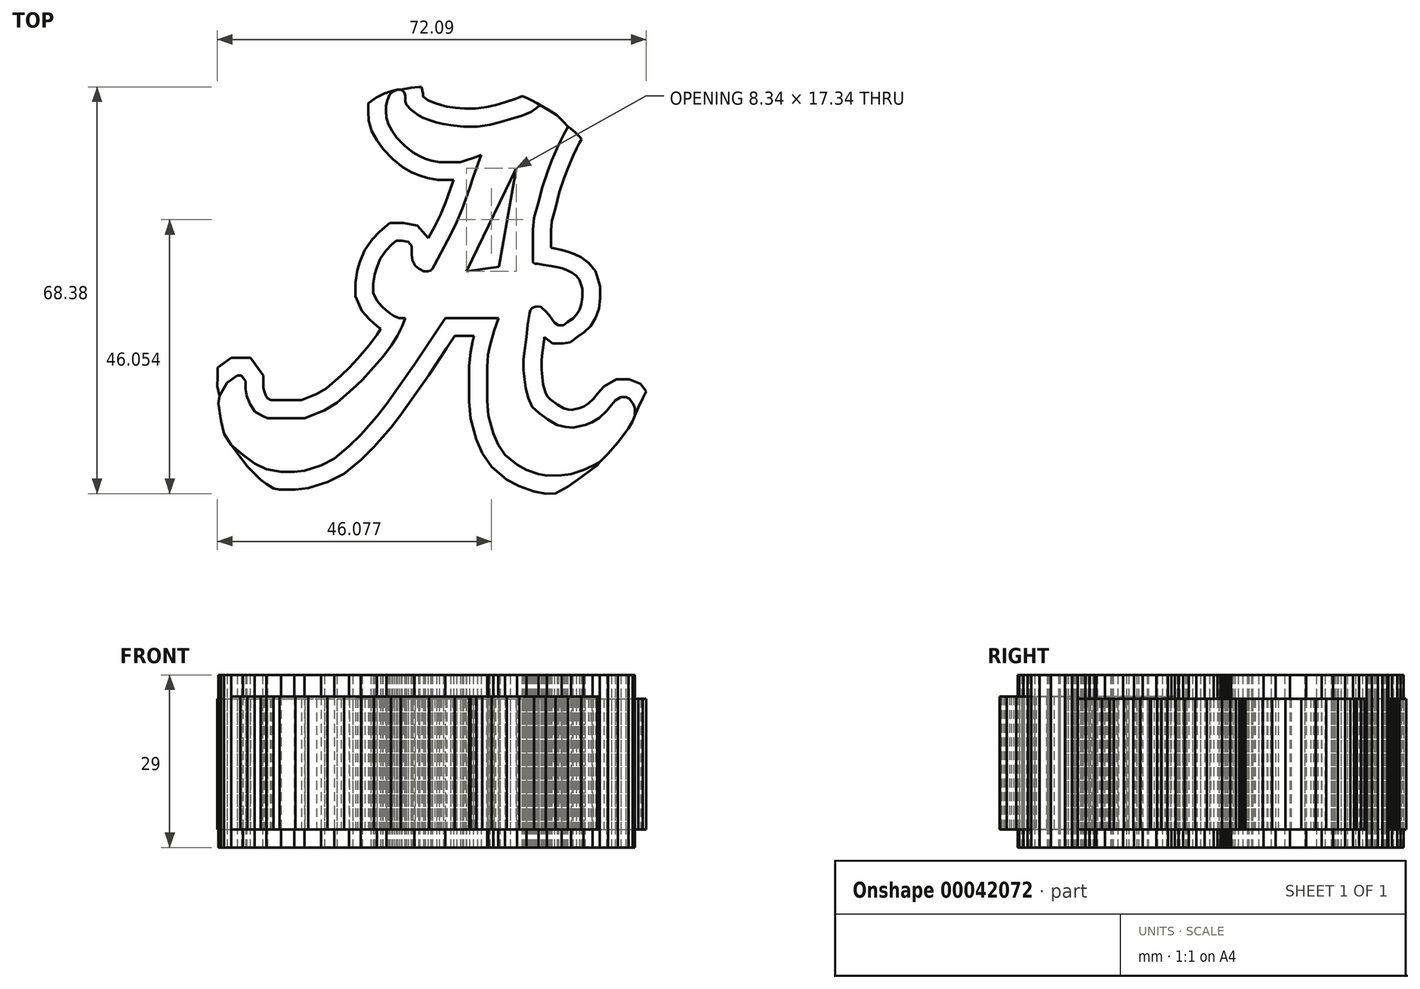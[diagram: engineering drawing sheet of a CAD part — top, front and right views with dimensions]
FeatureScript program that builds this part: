
annotation { "Feature Type Name" : "Feature", "Feature Type Description" : "" }
export const myFeature = defineFeature(function(context is Context, id is Id, definition is map)
    precondition{}
    {
        {
            var Q0;
            Q0=qCreatedBy(makeId("Top.planeOp"),FACE);
            var sketch = newSketch(context, id + "F0", { "sketchPlane" : qUnion([Q0])});
            skLineSegment(sketch, "E0", {"start": v(-56.78, -79.16) * mm, "end": v(-55.48, -76.91) * mm});
            skLineSegment(sketch, "E1", {"start": v(-55.48, -76.91) * mm, "end": v(-53.8, -75.71) * mm});
            skLineSegment(sketch, "E2", {"start": v(-53.8, -75.71) * mm, "end": v(-53.08, -75.71) * mm});
            skLineSegment(sketch, "E3", {"start": v(-53.08, -75.71) * mm, "end": v(-52.4, -76.66) * mm});
            skLineSegment(sketch, "E4", {"start": v(-52.4, -76.66) * mm, "end": v(-52.4, -78.02) * mm});
            skLineSegment(sketch, "E5", {"start": v(-52.4, -78.02) * mm, "end": v(-52.17, -79.12) * mm});
            skLineSegment(sketch, "E6", {"start": v(-52.17, -79.12) * mm, "end": v(-51.62, -80.55) * mm});
            skLineSegment(sketch, "E7", {"start": v(-51.62, -80.55) * mm, "end": v(-50.78, -81.82) * mm});
            skLineSegment(sketch, "E8", {"start": v(-50.78, -81.82) * mm, "end": v(-49.54, -82.5) * mm});
            skLineSegment(sketch, "E9", {"start": v(-49.54, -82.5) * mm, "end": v(-48.7, -82.86) * mm});
            skLineSegment(sketch, "E10", {"start": v(-48.7, -82.86) * mm, "end": v(-46.72, -82.86) * mm});
            skLineSegment(sketch, "E11", {"start": v(-46.72, -82.86) * mm, "end": v(-44.38, -82.86) * mm});
            skLineSegment(sketch, "E12", {"start": v(-44.38, -82.86) * mm, "end": v(-42.42, -82.86) * mm});
            skLineSegment(sketch, "E13", {"start": v(-42.42, -82.86) * mm, "end": v(-39.08, -81.54) * mm});
            skLineSegment(sketch, "E14", {"start": v(-39.08, -81.54) * mm, "end": v(-37.02, -80.29) * mm});
            skLineSegment(sketch, "E15", {"start": v(-37.02, -80.29) * mm, "end": v(-34.33, -77.96) * mm});
            skLineSegment(sketch, "E16", {"start": v(-34.33, -77.96) * mm, "end": v(-32.78, -76.5) * mm});
            skLineSegment(sketch, "E17", {"start": v(-32.78, -76.5) * mm, "end": v(-31.29, -74.85) * mm});
            skLineSegment(sketch, "E18", {"start": v(-31.29, -74.85) * mm, "end": v(-29.28, -72.52) * mm});
            skLineSegment(sketch, "E19", {"start": v(-29.28, -72.52) * mm, "end": v(-27.82, -70.57) * mm});
            skLineSegment(sketch, "E20", {"start": v(-27.82, -70.57) * mm, "end": v(-26.85, -69.02) * mm});
            skLineSegment(sketch, "E21", {"start": v(-26.85, -69.02) * mm, "end": v(-26.1, -67.53) * mm});
            skLineSegment(sketch, "E22", {"start": v(-26.1, -67.53) * mm, "end": v(-25.54, -66.05) * mm});
            skLineSegment(sketch, "E23", {"start": v(-25.54, -66.05) * mm, "end": v(-26.55, -66.05) * mm});
            skLineSegment(sketch, "E24", {"start": v(-26.55, -66.05) * mm, "end": v(-27.33, -65.75) * mm});
            skLineSegment(sketch, "E25", {"start": v(-27.33, -65.75) * mm, "end": v(-28.11, -65.26) * mm});
            skLineSegment(sketch, "E26", {"start": v(-28.11, -65.26) * mm, "end": v(-28.84, -64.67) * mm});
            skLineSegment(sketch, "E27", {"start": v(-28.84, -64.67) * mm, "end": v(-29.37, -64.14) * mm});
            skLineSegment(sketch, "E28", {"start": v(-29.37, -64.14) * mm, "end": v(-30.3, -63.15) * mm});
            skLineSegment(sketch, "E29", {"start": v(-30.3, -63.15) * mm, "end": v(-30.9, -61.77) * mm});
            skLineSegment(sketch, "E30", {"start": v(-30.9, -61.77) * mm, "end": v(-30.9, -60.3) * mm});
            skLineSegment(sketch, "E31", {"start": v(-30.9, -60.3) * mm, "end": v(-30.63, -58.7) * mm});
            skLineSegment(sketch, "E32", {"start": v(-30.63, -58.7) * mm, "end": v(-30.27, -57.51) * mm});
            skLineSegment(sketch, "E33", {"start": v(-30.27, -57.51) * mm, "end": v(-29.68, -56.03) * mm});
            skLineSegment(sketch, "E34", {"start": v(-29.68, -56.03) * mm, "end": v(-28.72, -54.68) * mm});
            skLineSegment(sketch, "E35", {"start": v(-28.72, -54.68) * mm, "end": v(-27.77, -53.7) * mm});
            skLineSegment(sketch, "E36", {"start": v(-27.77, -53.7) * mm, "end": v(-27.02, -53.04) * mm});
            skLineSegment(sketch, "E37", {"start": v(-27.02, -53.04) * mm, "end": v(-26.1, -53.04) * mm});
            skLineSegment(sketch, "E38", {"start": v(-26.1, -53.04) * mm, "end": v(-25.03, -53.24) * mm});
            skLineSegment(sketch, "E39", {"start": v(-25.03, -53.24) * mm, "end": v(-24.45, -53.91) * mm});
            skLineSegment(sketch, "E40", {"start": v(-24.45, -53.91) * mm, "end": v(-24.45, -54.89) * mm});
            skLineSegment(sketch, "E41", {"start": v(-24.45, -54.89) * mm, "end": v(-24.45, -55.44) * mm});
            skLineSegment(sketch, "E42", {"start": v(-24.45, -55.44) * mm, "end": v(-24.3, -56.31) * mm});
            skLineSegment(sketch, "E43", {"start": v(-24.3, -56.31) * mm, "end": v(-23.85, -57.26) * mm});
            skLineSegment(sketch, "E44", {"start": v(-23.85, -57.26) * mm, "end": v(-23.21, -57.73) * mm});
            skLineSegment(sketch, "E45", {"start": v(-23.21, -57.73) * mm, "end": v(-22.38, -58.21) * mm});
            skLineSegment(sketch, "E46", {"start": v(-22.38, -58.21) * mm, "end": v(-21.7, -58.21) * mm});
            skLineSegment(sketch, "E47", {"start": v(-21.7, -58.21) * mm, "end": v(-21.23, -58.04) * mm});
            skLineSegment(sketch, "E48", {"start": v(-21.23, -58.04) * mm, "end": v(-20.94, -57.73) * mm});
            skLineSegment(sketch, "E49", {"start": v(-20.94, -57.73) * mm, "end": v(-20.58, -57.05) * mm});
            skLineSegment(sketch, "E50", {"start": v(-20.58, -57.05) * mm, "end": v(-17.92, -52.02) * mm});
            skLineSegment(sketch, "E51", {"start": v(-17.92, -52.02) * mm, "end": v(-16.88, -49.93) * mm});
            skLineSegment(sketch, "E52", {"start": v(-16.88, -49.93) * mm, "end": v(-15.93, -47.62) * mm});
            skLineSegment(sketch, "E53", {"start": v(-15.93, -47.62) * mm, "end": v(-14.72, -44.27) * mm});
            skLineSegment(sketch, "E54", {"start": v(-14.72, -44.27) * mm, "end": v(-14.08, -42.31) * mm});
            skLineSegment(sketch, "E55", {"start": v(-14.08, -42.31) * mm, "end": v(-12.77, -38.62) * mm});
            skLineSegment(sketch, "E56", {"start": v(-12.77, -38.62) * mm, "end": v(-14.08, -39.13) * mm});
            skLineSegment(sketch, "E57", {"start": v(-14.08, -39.13) * mm, "end": v(-15.3, -39.54) * mm});
            skLineSegment(sketch, "E58", {"start": v(-15.3, -39.54) * mm, "end": v(-16.22, -39.8) * mm});
            skLineSegment(sketch, "E59", {"start": v(-16.22, -39.8) * mm, "end": v(-17.38, -39.8) * mm});
            skLineSegment(sketch, "E60", {"start": v(-17.38, -39.8) * mm, "end": v(-18.8, -39.8) * mm});
            skLineSegment(sketch, "E61", {"start": v(-18.8, -39.8) * mm, "end": v(-19.8, -39.8) * mm});
            skLineSegment(sketch, "E62", {"start": v(-19.8, -39.8) * mm, "end": v(-21.1, -39.57) * mm});
            skLineSegment(sketch, "E63", {"start": v(-21.1, -39.57) * mm, "end": v(-22.14, -39.26) * mm});
            skLineSegment(sketch, "E64", {"start": v(-22.14, -39.26) * mm, "end": v(-23.1, -38.83) * mm});
            skLineSegment(sketch, "E65", {"start": v(-23.1, -38.83) * mm, "end": v(-24.24, -38.2) * mm});
            skLineSegment(sketch, "E66", {"start": v(-24.24, -38.2) * mm, "end": v(-25.57, -37.13) * mm});
            skLineSegment(sketch, "E67", {"start": v(-25.57, -37.13) * mm, "end": v(-26.95, -35.69) * mm});
            skLineSegment(sketch, "E68", {"start": v(-26.95, -35.69) * mm, "end": v(-27.71, -34.57) * mm});
            skLineSegment(sketch, "E69", {"start": v(-27.71, -34.57) * mm, "end": v(-28.36, -33.43) * mm});
            skLineSegment(sketch, "E70", {"start": v(-28.36, -33.43) * mm, "end": v(-28.68, -32.32) * mm});
            skLineSegment(sketch, "E71", {"start": v(-28.68, -32.32) * mm, "end": v(-28.74, -31.26) * mm});
            skLineSegment(sketch, "E72", {"start": v(-28.74, -31.26) * mm, "end": v(-28.74, -30.32) * mm});
            skLineSegment(sketch, "E73", {"start": v(-28.74, -30.32) * mm, "end": v(-28.5, -29.39) * mm});
            skLineSegment(sketch, "E74", {"start": v(-28.5, -29.39) * mm, "end": v(-28.18, -28.54) * mm});
            skLineSegment(sketch, "E75", {"start": v(-28.18, -28.54) * mm, "end": v(-27.7, -28.04) * mm});
            skLineSegment(sketch, "E76", {"start": v(-27.7, -28.04) * mm, "end": v(-26.86, -27.64) * mm});
            skLineSegment(sketch, "E77", {"start": v(-26.86, -27.64) * mm, "end": v(-26.2, -27.64) * mm});
            skLineSegment(sketch, "E78", {"start": v(-26.2, -27.64) * mm, "end": v(-25.65, -28.15) * mm});
            skLineSegment(sketch, "E79", {"start": v(-25.65, -28.15) * mm, "end": v(-25.5, -28.75) * mm});
            skLineSegment(sketch, "E80", {"start": v(-25.5, -28.75) * mm, "end": v(-25.5, -29.6) * mm});
            skLineSegment(sketch, "E81", {"start": v(-25.5, -29.6) * mm, "end": v(-25.3, -30.2) * mm});
            skLineSegment(sketch, "E82", {"start": v(-25.3, -30.2) * mm, "end": v(-24.55, -31) * mm});
            skLineSegment(sketch, "E83", {"start": v(-24.55, -31) * mm, "end": v(-23.32, -31.94) * mm});
            skLineSegment(sketch, "E84", {"start": v(-23.32, -31.94) * mm, "end": v(-22.49, -32.39) * mm});
            skLineSegment(sketch, "E85", {"start": v(-22.49, -32.39) * mm, "end": v(-21.4, -32.76) * mm});
            skLineSegment(sketch, "E86", {"start": v(-21.4, -32.76) * mm, "end": v(-20.26, -33.15) * mm});
            skLineSegment(sketch, "E87", {"start": v(-20.26, -33.15) * mm, "end": v(-19.1, -33.43) * mm});
            skLineSegment(sketch, "E88", {"start": v(-19.1, -33.43) * mm, "end": v(-17.4, -33.67) * mm});
            skLineSegment(sketch, "E89", {"start": v(-17.4, -33.67) * mm, "end": v(-15.71, -33.84) * mm});
            skLineSegment(sketch, "E90", {"start": v(-15.71, -33.84) * mm, "end": v(-13.96, -33.84) * mm});
            skLineSegment(sketch, "E91", {"start": v(-13.96, -33.84) * mm, "end": v(-13.39, -33.84) * mm});
            skLineSegment(sketch, "E92", {"start": v(-13.39, -33.84) * mm, "end": v(-11.31, -33.52) * mm});
            skLineSegment(sketch, "E93", {"start": v(-11.31, -33.52) * mm, "end": v(-9.59, -33.13) * mm});
            skLineSegment(sketch, "E94", {"start": v(-9.59, -33.13) * mm, "end": v(-7.84, -32.61) * mm});
            skLineSegment(sketch, "E95", {"start": v(-7.84, -32.61) * mm, "end": v(-5.91, -32) * mm});
            skLineSegment(sketch, "E96", {"start": v(-5.91, -32) * mm, "end": v(-4.4, -31.38) * mm});
            skLineSegment(sketch, "E97", {"start": v(-4.4, -31.38) * mm, "end": v(-3.48, -30.75) * mm});
            skLineSegment(sketch, "E98", {"start": v(-3.48, -30.75) * mm, "end": v(-3.06, -30.35) * mm});
            skLineSegment(sketch, "E99", {"start": v(-3.06, -30.35) * mm, "end": v(-2.62, -30.35) * mm});
            skLineSegment(sketch, "E100", {"start": v(-2.62, -30.35) * mm, "end": v(-1.19, -31.17) * mm});
            skLineSegment(sketch, "E101", {"start": v(-1.19, -31.17) * mm, "end": v(0, -31.98) * mm});
            skLineSegment(sketch, "E102", {"start": v(0, -31.98) * mm, "end": v(1.02, -32.97) * mm});
            skLineSegment(sketch, "E103", {"start": v(1.02, -32.97) * mm, "end": v(1.87, -33.88) * mm});
            skLineSegment(sketch, "E104", {"start": v(1.87, -33.88) * mm, "end": v(1.15, -35.16) * mm});
            skLineSegment(sketch, "E105", {"start": v(1.15, -35.16) * mm, "end": v(0.63, -36.14) * mm});
            skLineSegment(sketch, "E106", {"start": v(0.63, -36.14) * mm, "end": v(0, -37.46) * mm});
            skLineSegment(sketch, "E107", {"start": v(0, -37.46) * mm, "end": v(-0.86, -39.54) * mm});
            skLineSegment(sketch, "E108", {"start": v(-0.86, -39.54) * mm, "end": v(-1.58, -41.4) * mm});
            skLineSegment(sketch, "E109", {"start": v(-1.58, -41.4) * mm, "end": v(-2.47, -44.03) * mm});
            skLineSegment(sketch, "E110", {"start": v(-2.47, -44.03) * mm, "end": v(-3.14, -46.76) * mm});
            skLineSegment(sketch, "E111", {"start": v(-3.14, -46.76) * mm, "end": v(-3.83, -49.14) * mm});
            skLineSegment(sketch, "E112", {"start": v(-3.83, -49.14) * mm, "end": v(-4.03, -51.18) * mm});
            skLineSegment(sketch, "E113", {"start": v(-4.03, -51.18) * mm, "end": v(-4.03, -53.63) * mm});
            skLineSegment(sketch, "E114", {"start": v(-4.03, -53.63) * mm, "end": v(-4.03, -55.63) * mm});
            skLineSegment(sketch, "E115", {"start": v(-4.03, -55.63) * mm, "end": v(-4.03, -56.36) * mm});
            skLineSegment(sketch, "E116", {"start": v(-4.03, -56.36) * mm, "end": v(-4.03, -56.69) * mm});
            skLineSegment(sketch, "E117", {"start": v(-4.03, -56.69) * mm, "end": v(-3.74, -56.9) * mm});
            skLineSegment(sketch, "E118", {"start": v(-3.74, -56.9) * mm, "end": v(-3.25, -56.9) * mm});
            skLineSegment(sketch, "E119", {"start": v(-3.25, -56.9) * mm, "end": v(-2.27, -57.1) * mm});
            skLineSegment(sketch, "E120", {"start": v(-2.27, -57.1) * mm, "end": v(-1.01, -57.3) * mm});
            skLineSegment(sketch, "E121", {"start": v(-1.01, -57.3) * mm, "end": v(0, -57.47) * mm});
            skLineSegment(sketch, "E122", {"start": v(0, -57.47) * mm, "end": v(0.87, -57.7) * mm});
            skLineSegment(sketch, "E123", {"start": v(0.87, -57.7) * mm, "end": v(1.67, -58.01) * mm});
            skLineSegment(sketch, "E124", {"start": v(1.67, -58.01) * mm, "end": v(2.56, -58.43) * mm});
            skLineSegment(sketch, "E125", {"start": v(2.56, -58.43) * mm, "end": v(3.27, -58.95) * mm});
            skLineSegment(sketch, "E126", {"start": v(3.27, -58.95) * mm, "end": v(3.79, -59.6) * mm});
            skLineSegment(sketch, "E127", {"start": v(3.79, -59.6) * mm, "end": v(3.98, -60.24) * mm});
            skLineSegment(sketch, "E128", {"start": v(3.98, -60.24) * mm, "end": v(4.24, -61.14) * mm});
            skLineSegment(sketch, "E129", {"start": v(4.24, -61.14) * mm, "end": v(4.24, -62.5) * mm});
            skLineSegment(sketch, "E130", {"start": v(4.24, -62.5) * mm, "end": v(4.1, -63.77) * mm});
            skLineSegment(sketch, "E131", {"start": v(4.1, -63.77) * mm, "end": v(3.75, -64.7) * mm});
            skLineSegment(sketch, "E132", {"start": v(3.75, -64.7) * mm, "end": v(3.27, -65.5) * mm});
            skLineSegment(sketch, "E133", {"start": v(3.27, -65.5) * mm, "end": v(2.67, -66.1) * mm});
            skLineSegment(sketch, "E134", {"start": v(2.67, -66.1) * mm, "end": v(1.82, -66.67) * mm});
            skLineSegment(sketch, "E135", {"start": v(1.82, -66.67) * mm, "end": v(1.06, -67.25) * mm});
            skLineSegment(sketch, "E136", {"start": v(1.06, -67.25) * mm, "end": v(0.8, -67.28) * mm});
            skLineSegment(sketch, "E137", {"start": v(0.8, -67.28) * mm, "end": v(0.25, -67.28) * mm});
            skLineSegment(sketch, "E138", {"start": v(0.25, -67.28) * mm, "end": v(-0.4, -66.8) * mm});
            skLineSegment(sketch, "E139", {"start": v(-0.4, -66.8) * mm, "end": v(-1.34, -65.52) * mm});
            skLineSegment(sketch, "E140", {"start": v(-1.34, -65.52) * mm, "end": v(-2, -64.82) * mm});
            skLineSegment(sketch, "E141", {"start": v(-2, -64.82) * mm, "end": v(-2.37, -64.45) * mm});
            skLineSegment(sketch, "E142", {"start": v(-2.37, -64.45) * mm, "end": v(-2.7, -64.18) * mm});
            skLineSegment(sketch, "E143", {"start": v(-2.7, -64.18) * mm, "end": v(-3.23, -64.11) * mm});
            skLineSegment(sketch, "E144", {"start": v(-3.23, -64.11) * mm, "end": v(-3.66, -64.13) * mm});
            skLineSegment(sketch, "E145", {"start": v(-3.66, -64.13) * mm, "end": v(-4.18, -64.33) * mm});
            skLineSegment(sketch, "E146", {"start": v(-4.18, -64.33) * mm, "end": v(-4.5, -64.75) * mm});
            skLineSegment(sketch, "E147", {"start": v(-4.5, -64.75) * mm, "end": v(-4.64, -65.28) * mm});
            skLineSegment(sketch, "E148", {"start": v(-4.64, -65.28) * mm, "end": v(-4.94, -67.2) * mm});
            skLineSegment(sketch, "E149", {"start": v(-4.94, -67.2) * mm, "end": v(-5.14, -69.25) * mm});
            skLineSegment(sketch, "E150", {"start": v(-5.14, -69.25) * mm, "end": v(-5.46, -71.5) * mm});
            skLineSegment(sketch, "E151", {"start": v(-5.46, -71.5) * mm, "end": v(-5.62, -72.96) * mm});
            skLineSegment(sketch, "E152", {"start": v(-5.62, -72.96) * mm, "end": v(-5.62, -74.84) * mm});
            skLineSegment(sketch, "E153", {"start": v(-5.62, -74.84) * mm, "end": v(-5.28, -77.85) * mm});
            skLineSegment(sketch, "E154", {"start": v(-5.28, -77.85) * mm, "end": v(-4.8, -79.5) * mm});
            skLineSegment(sketch, "E155", {"start": v(-4.8, -79.5) * mm, "end": v(-4.16, -80.97) * mm});
            skLineSegment(sketch, "E156", {"start": v(-4.16, -80.97) * mm, "end": v(-3.03, -82.02) * mm});
            skLineSegment(sketch, "E157", {"start": v(-3.03, -82.02) * mm, "end": v(-1.58, -83.1) * mm});
            skLineSegment(sketch, "E158", {"start": v(-1.58, -83.1) * mm, "end": v(0, -84.01) * mm});
            skLineSegment(sketch, "E159", {"start": v(0, -84.01) * mm, "end": v(1.41, -84.38) * mm});
            skLineSegment(sketch, "E160", {"start": v(1.41, -84.38) * mm, "end": v(2.69, -84.48) * mm});
            skLineSegment(sketch, "E161", {"start": v(2.69, -84.48) * mm, "end": v(4.7, -84.05) * mm});
            skLineSegment(sketch, "E162", {"start": v(4.7, -84.05) * mm, "end": v(5.86, -83.59) * mm});
            skLineSegment(sketch, "E163", {"start": v(5.86, -83.59) * mm, "end": v(7.11, -82.81) * mm});
            skLineSegment(sketch, "E164", {"start": v(7.11, -82.81) * mm, "end": v(8.32, -81.7) * mm});
            skLineSegment(sketch, "E165", {"start": v(8.32, -81.7) * mm, "end": v(9.13, -80.65) * mm});
            skLineSegment(sketch, "E166", {"start": v(9.13, -80.65) * mm, "end": v(9.8, -79.88) * mm});
            skLineSegment(sketch, "E167", {"start": v(9.8, -79.88) * mm, "end": v(10.75, -79.34) * mm});
            skLineSegment(sketch, "E168", {"start": v(10.75, -79.34) * mm, "end": v(11.55, -79.34) * mm});
            skLineSegment(sketch, "E169", {"start": v(11.55, -79.34) * mm, "end": v(12.12, -79.58) * mm});
            skLineSegment(sketch, "E170", {"start": v(12.12, -79.58) * mm, "end": v(12.77, -80.44) * mm});
            skLineSegment(sketch, "E171", {"start": v(12.77, -80.44) * mm, "end": v(13.1, -81.15) * mm});
            skLineSegment(sketch, "E172", {"start": v(13.1, -81.15) * mm, "end": v(13.1, -82.44) * mm});
            skLineSegment(sketch, "E173", {"start": v(13.1, -82.44) * mm, "end": v(12.73, -83.4) * mm});
            skLineSegment(sketch, "E174", {"start": v(12.73, -83.4) * mm, "end": v(12.02, -84.6) * mm});
            skLineSegment(sketch, "E175", {"start": v(12.02, -84.6) * mm, "end": v(10.26, -86.95) * mm});
            skLineSegment(sketch, "E176", {"start": v(10.26, -86.95) * mm, "end": v(8.58, -88.86) * mm});
            skLineSegment(sketch, "E177", {"start": v(8.58, -88.86) * mm, "end": v(7.21, -90.23) * mm});
            skLineSegment(sketch, "E178", {"start": v(7.21, -90.23) * mm, "end": v(6, -90.88) * mm});
            skLineSegment(sketch, "E179", {"start": v(6, -90.88) * mm, "end": v(4.46, -91.56) * mm});
            skLineSegment(sketch, "E180", {"start": v(4.46, -91.56) * mm, "end": v(2.38, -92.27) * mm});
            skLineSegment(sketch, "E181", {"start": v(2.38, -92.27) * mm, "end": v(0.8, -92.45) * mm});
            skLineSegment(sketch, "E182", {"start": v(0.8, -92.45) * mm, "end": v(-1.68, -92.55) * mm});
            skLineSegment(sketch, "E183", {"start": v(-1.68, -92.55) * mm, "end": v(-3.09, -92.3) * mm});
            skLineSegment(sketch, "E184", {"start": v(-3.09, -92.3) * mm, "end": v(-5.15, -91.57) * mm});
            skLineSegment(sketch, "E185", {"start": v(-5.15, -91.57) * mm, "end": v(-6.73, -90.72) * mm});
            skLineSegment(sketch, "E186", {"start": v(-6.73, -90.72) * mm, "end": v(-8.73, -89.06) * mm});
            skLineSegment(sketch, "E187", {"start": v(-8.73, -89.06) * mm, "end": v(-9.9, -87.32) * mm});
            skLineSegment(sketch, "E188", {"start": v(-9.9, -87.32) * mm, "end": v(-10.72, -85.44) * mm});
            skLineSegment(sketch, "E189", {"start": v(-10.72, -85.44) * mm, "end": v(-11.55, -82.41) * mm});
            skLineSegment(sketch, "E190", {"start": v(-11.55, -82.41) * mm, "end": v(-11.77, -79.93) * mm});
            skLineSegment(sketch, "E191", {"start": v(-11.77, -79.93) * mm, "end": v(-11.77, -77.61) * mm});
            skLineSegment(sketch, "E192", {"start": v(-11.77, -77.61) * mm, "end": v(-11.77, -74.25) * mm});
            skLineSegment(sketch, "E193", {"start": v(-11.77, -74.25) * mm, "end": v(-11.58, -72.22) * mm});
            skLineSegment(sketch, "E194", {"start": v(-11.58, -72.22) * mm, "end": v(-11.29, -70.75) * mm});
            skLineSegment(sketch, "E195", {"start": v(-11.29, -70.75) * mm, "end": v(-10.6, -68.2) * mm});
            skLineSegment(sketch, "E196", {"start": v(-10.6, -68.2) * mm, "end": v(-9.82, -66.04) * mm});
            skLineSegment(sketch, "E197", {"start": v(-9.82, -66.04) * mm, "end": v(-18.8, -66.04) * mm});
            skLineSegment(sketch, "E198", {"start": v(-18.8, -66.04) * mm, "end": v(-21.06, -69.46) * mm});
            skLineSegment(sketch, "E199", {"start": v(-21.06, -69.46) * mm, "end": v(-24, -73.86) * mm});
            skLineSegment(sketch, "E200", {"start": v(-24, -73.86) * mm, "end": v(-28.68, -80.52) * mm});
            skLineSegment(sketch, "E201", {"start": v(-28.68, -80.52) * mm, "end": v(-30.27, -82.55) * mm});
            skLineSegment(sketch, "E202", {"start": v(-30.27, -82.55) * mm, "end": v(-32.99, -85.67) * mm});
            skLineSegment(sketch, "E203", {"start": v(-32.99, -85.67) * mm, "end": v(-34.96, -87.61) * mm});
            skLineSegment(sketch, "E204", {"start": v(-34.96, -87.61) * mm, "end": v(-37.47, -89.7) * mm});
            skLineSegment(sketch, "E205", {"start": v(-37.47, -89.7) * mm, "end": v(-39.7, -90.83) * mm});
            skLineSegment(sketch, "E206", {"start": v(-39.7, -90.83) * mm, "end": v(-42.48, -91.7) * mm});
            skLineSegment(sketch, "E207", {"start": v(-42.48, -91.7) * mm, "end": v(-44.19, -91.9) * mm});
            skLineSegment(sketch, "E208", {"start": v(-44.19, -91.9) * mm, "end": v(-46.4, -91.9) * mm});
            skLineSegment(sketch, "E209", {"start": v(-46.4, -91.9) * mm, "end": v(-48.86, -91.47) * mm});
            skLineSegment(sketch, "E210", {"start": v(-48.86, -91.47) * mm, "end": v(-50.85, -90.5) * mm});
            skLineSegment(sketch, "E211", {"start": v(-50.85, -90.5) * mm, "end": v(-52.83, -89.02) * mm});
            skLineSegment(sketch, "E212", {"start": v(-52.83, -89.02) * mm, "end": v(-54.82, -87.41) * mm});
            skLineSegment(sketch, "E213", {"start": v(-54.82, -87.41) * mm, "end": v(-56.03, -85.46) * mm});
            skLineSegment(sketch, "E214", {"start": v(-56.03, -85.46) * mm, "end": v(-56.53, -83.33) * mm});
            skLineSegment(sketch, "E215", {"start": v(-56.53, -83.33) * mm, "end": v(-56.93, -80.38) * mm});
            skLineSegment(sketch, "E216", {"start": v(-56.93, -80.38) * mm, "end": v(-56.78, -79.16) * mm});
            skLineSegment(sketch, "E217", {"start": v(-15.2, -58.18) * mm, "end": v(-6.86, -40.83) * mm});
            skLineSegment(sketch, "E218", {"start": v(-6.86, -40.83) * mm, "end": v(-9.76, -57.44) * mm});
            skLineSegment(sketch, "E219", {"start": v(-15.2, -58.18) * mm, "end": v(-9.76, -57.44) * mm});
            skLineSegment(sketch, "E220.0", {"start": v(-27.6, -39.34) * mm, "end": v(-29.29, -37.58) * mm});
            skLineSegment(sketch, "E220.1", {"start": v(-25.92, -40.7) * mm, "end": v(-27.6, -39.34) * mm});
            skLineSegment(sketch, "E220.2", {"start": v(-24.44, -41.52) * mm, "end": v(-25.92, -40.7) * mm});
            skLineSegment(sketch, "E220.3", {"start": v(-23.2, -42.08) * mm, "end": v(-24.44, -41.52) * mm});
            skLineSegment(sketch, "E220.4", {"start": v(-21.8, -42.5) * mm, "end": v(-23.2, -42.08) * mm});
            skLineSegment(sketch, "E220.5", {"start": v(-20.05, -42.8) * mm, "end": v(-21.8, -42.5) * mm});
            skLineSegment(sketch, "E220.6", {"start": v(-18.8, -42.8) * mm, "end": v(-20.05, -42.8) * mm});
            skLineSegment(sketch, "E220.7", {"start": v(-17.4, -42.8) * mm, "end": v(-18.8, -42.8) * mm});
            skLineSegment(sketch, "E220.8", {"start": v(-17.56, -43.3) * mm, "end": v(-17.4, -42.8) * mm});
            skLineSegment(sketch, "E220.9", {"start": v(-18.73, -46.54) * mm, "end": v(-17.56, -43.3) * mm});
            skLineSegment(sketch, "E220.10", {"start": v(-19.62, -48.7) * mm, "end": v(-18.73, -46.54) * mm});
            skLineSegment(sketch, "E220.11", {"start": v(-20.59, -50.65) * mm, "end": v(-19.62, -48.7) * mm});
            skLineSegment(sketch, "E220.12", {"start": v(-21.62, -52.59) * mm, "end": v(-20.59, -50.65) * mm});
            skLineSegment(sketch, "E220.13", {"start": v(-23.46, -50.49) * mm, "end": v(-21.62, -52.59) * mm});
            skLineSegment(sketch, "E220.14", {"start": v(-25.8, -50.04) * mm, "end": v(-23.46, -50.49) * mm});
            skLineSegment(sketch, "E220.15", {"start": v(-28.13, -50.04) * mm, "end": v(-25.8, -50.04) * mm});
            skLineSegment(sketch, "E220.16", {"start": v(-29.83, -51.51) * mm, "end": v(-28.13, -50.04) * mm});
            skLineSegment(sketch, "E220.17", {"start": v(-31.04, -52.76) * mm, "end": v(-29.83, -51.51) * mm});
            skLineSegment(sketch, "E220.18", {"start": v(-32.33, -54.6) * mm, "end": v(-31.04, -52.76) * mm});
            skLineSegment(sketch, "E220.19", {"start": v(-33.1, -56.52) * mm, "end": v(-32.33, -54.6) * mm});
            skLineSegment(sketch, "E220.20", {"start": v(-33.56, -58.01) * mm, "end": v(-33.1, -56.52) * mm});
            skLineSegment(sketch, "E220.21", {"start": v(-33.9, -60.06) * mm, "end": v(-33.56, -58.01) * mm});
            skLineSegment(sketch, "E220.22", {"start": v(-33.9, -62.4) * mm, "end": v(-33.9, -60.06) * mm});
            skLineSegment(sketch, "E220.23", {"start": v(-32.83, -64.82) * mm, "end": v(-33.9, -62.4) * mm});
            skLineSegment(sketch, "E220.24", {"start": v(-31.52, -66.23) * mm, "end": v(-32.83, -64.82) * mm});
            skLineSegment(sketch, "E220.25", {"start": v(-30.86, -66.9) * mm, "end": v(-31.52, -66.23) * mm});
            skLineSegment(sketch, "E220.26", {"start": v(-29.87, -67.7) * mm, "end": v(-30.86, -66.9) * mm});
            skLineSegment(sketch, "E220.27", {"start": v(-29.65, -67.84) * mm, "end": v(-29.87, -67.7) * mm});
            skLineSegment(sketch, "E220.28", {"start": v(-30.3, -68.88) * mm, "end": v(-29.65, -67.84) * mm});
            skLineSegment(sketch, "E220.29", {"start": v(-31.62, -70.63) * mm, "end": v(-30.3, -68.88) * mm});
            skLineSegment(sketch, "E220.30", {"start": v(-33.54, -72.87) * mm, "end": v(-31.62, -70.63) * mm});
            skLineSegment(sketch, "E220.31", {"start": v(-34.92, -74.4) * mm, "end": v(-33.54, -72.87) * mm});
            skLineSegment(sketch, "E220.32", {"start": v(-36.34, -75.73) * mm, "end": v(-34.92, -74.4) * mm});
            skLineSegment(sketch, "E220.33", {"start": v(-38.8, -77.86) * mm, "end": v(-36.34, -75.73) * mm});
            skLineSegment(sketch, "E220.34", {"start": v(-40.42, -78.85) * mm, "end": v(-38.8, -77.86) * mm});
            skLineSegment(sketch, "E220.35", {"start": v(-43, -79.86) * mm, "end": v(-40.42, -78.85) * mm});
            skLineSegment(sketch, "E220.36", {"start": v(-44.38, -79.86) * mm, "end": v(-43, -79.86) * mm});
            skLineSegment(sketch, "E220.37", {"start": v(-46.72, -79.86) * mm, "end": v(-44.38, -79.86) * mm});
            skLineSegment(sketch, "E220.38", {"start": v(-48.09, -79.86) * mm, "end": v(-46.72, -79.86) * mm});
            skLineSegment(sketch, "E220.39", {"start": v(-48.22, -79.8) * mm, "end": v(-48.09, -79.86) * mm});
            skLineSegment(sketch, "E220.40", {"start": v(-48.69, -79.55) * mm, "end": v(-48.22, -79.8) * mm});
            skLineSegment(sketch, "E220.41", {"start": v(-48.94, -79.16) * mm, "end": v(-48.69, -79.55) * mm});
            skLineSegment(sketch, "E220.42", {"start": v(-49.28, -78.28) * mm, "end": v(-48.94, -79.16) * mm});
            skLineSegment(sketch, "E220.43", {"start": v(-49.4, -77.71) * mm, "end": v(-49.28, -78.28) * mm});
            skLineSegment(sketch, "E220.44", {"start": v(-49.4, -75.69) * mm, "end": v(-49.4, -77.71) * mm});
            skLineSegment(sketch, "E220.45", {"start": v(-51.54, -72.71) * mm, "end": v(-49.4, -75.69) * mm});
            skLineSegment(sketch, "E220.46", {"start": v(-54.76, -72.71) * mm, "end": v(-51.54, -72.71) * mm});
            skLineSegment(sketch, "E220.47", {"start": v(-57.1, -74.38) * mm, "end": v(-54.76, -72.71) * mm});
            skLineSegment(sketch, "E220.49", {"start": v(-29.29, -37.58) * mm, "end": v(-30.26, -36.16) * mm});
            skLineSegment(sketch, "E220.57", {"start": v(-46.66, -94.9) * mm, "end": v(-47.7, -94.72) * mm});
            skLineSegment(sketch, "E220.58", {"start": v(-44, -94.9) * mm, "end": v(-46.66, -94.9) * mm});
            skLineSegment(sketch, "E220.59", {"start": v(-41.84, -94.65) * mm, "end": v(-44, -94.9) * mm});
            skLineSegment(sketch, "E220.60", {"start": v(-38.57, -93.61) * mm, "end": v(-41.84, -94.65) * mm});
            skLineSegment(sketch, "E220.61", {"start": v(-35.82, -92.22) * mm, "end": v(-38.57, -93.61) * mm});
            skLineSegment(sketch, "E220.62", {"start": v(-32.94, -89.84) * mm, "end": v(-35.82, -92.22) * mm});
            skLineSegment(sketch, "E220.63", {"start": v(-30.8, -87.73) * mm, "end": v(-32.94, -89.84) * mm});
            skLineSegment(sketch, "E220.64", {"start": v(-27.96, -84.46) * mm, "end": v(-30.8, -87.73) * mm});
            skLineSegment(sketch, "E220.65", {"start": v(-26.27, -82.31) * mm, "end": v(-27.96, -84.46) * mm});
            skLineSegment(sketch, "E220.66", {"start": v(-21.52, -75.55) * mm, "end": v(-26.27, -82.31) * mm});
            skLineSegment(sketch, "E220.67", {"start": v(-18.56, -71.12) * mm, "end": v(-21.52, -75.55) * mm});
            skLineSegment(sketch, "E220.68", {"start": v(-17.19, -69.04) * mm, "end": v(-18.56, -71.12) * mm});
            skLineSegment(sketch, "E220.69", {"start": v(-13.93, -69.04) * mm, "end": v(-17.19, -69.04) * mm});
            skLineSegment(sketch, "E220.70", {"start": v(-14.21, -70.06) * mm, "end": v(-13.93, -69.04) * mm});
            skLineSegment(sketch, "E220.71", {"start": v(-14.56, -71.79) * mm, "end": v(-14.21, -70.06) * mm});
            skLineSegment(sketch, "E220.72", {"start": v(-14.77, -74.12) * mm, "end": v(-14.56, -71.79) * mm});
            skLineSegment(sketch, "E220.73", {"start": v(-14.77, -77.61) * mm, "end": v(-14.77, -74.12) * mm});
            skLineSegment(sketch, "E220.74", {"start": v(-14.77, -80.07) * mm, "end": v(-14.77, -77.61) * mm});
            skLineSegment(sketch, "E220.75", {"start": v(-14.51, -82.94) * mm, "end": v(-14.77, -80.07) * mm});
            skLineSegment(sketch, "E220.76", {"start": v(-13.56, -86.45) * mm, "end": v(-14.51, -82.94) * mm});
            skLineSegment(sketch, "E220.77", {"start": v(-12.53, -88.77) * mm, "end": v(-13.56, -86.45) * mm});
            skLineSegment(sketch, "E220.78", {"start": v(-10.98, -91.09) * mm, "end": v(-12.53, -88.77) * mm});
            skLineSegment(sketch, "E220.79", {"start": v(-8.42, -93.22) * mm, "end": v(-10.98, -91.09) * mm});
            skLineSegment(sketch, "E220.80", {"start": v(-6.36, -94.32) * mm, "end": v(-8.42, -93.22) * mm});
            skLineSegment(sketch, "E220.81", {"start": v(-3.85, -95.21) * mm, "end": v(-6.36, -94.32) * mm});
            skLineSegment(sketch, "E220.82", {"start": v(-1.88, -95.56) * mm, "end": v(-3.85, -95.21) * mm});
            skLineSegment(sketch, "E220.83", {"start": v(-0.24, -95.5) * mm, "end": v(-1.88, -95.56) * mm});
            skLineSegment(sketch, "E220.84", {"start": v(-0.53, -54.33) * mm, "end": v(0.65, -54.54) * mm});
            skLineSegment(sketch, "E220.85", {"start": v(-1.03, -54.26) * mm, "end": v(-0.53, -54.33) * mm});
            skLineSegment(sketch, "E220.86", {"start": v(-1.03, -53.63) * mm, "end": v(-1.03, -54.26) * mm});
            skLineSegment(sketch, "E220.87", {"start": v(-1.03, -51.33) * mm, "end": v(-1.03, -53.63) * mm});
            skLineSegment(sketch, "E220.88", {"start": v(-0.87, -49.71) * mm, "end": v(-1.03, -51.33) * mm});
            skLineSegment(sketch, "E220.89", {"start": v(-0.24, -47.54) * mm, "end": v(-0.87, -49.71) * mm});
            skLineSegment(sketch, "E220.90", {"start": v(0.42, -44.87) * mm, "end": v(-0.24, -47.54) * mm});
            skLineSegment(sketch, "E220.91", {"start": v(1.25, -42.42) * mm, "end": v(0.42, -44.87) * mm});
            skLineSegment(sketch, "E220.92", {"start": v(1.93, -40.65) * mm, "end": v(1.25, -42.42) * mm});
            skLineSegment(sketch, "E220.93", {"start": v(2.74, -38.68) * mm, "end": v(1.93, -40.65) * mm});
            skLineSegment(sketch, "E220.94", {"start": v(3.31, -37.5) * mm, "end": v(2.74, -38.68) * mm});
            skLineSegment(sketch, "E220.95", {"start": v(3.79, -36.6) * mm, "end": v(3.31, -37.5) * mm});
            skLineSegment(sketch, "E220.96", {"start": v(4.16, -35.94) * mm, "end": v(3.79, -36.6) * mm});
            skLineSegment(sketch, "E220.104", {"start": v(-6.93, -29.18) * mm, "end": v(-5.83, -28.73) * mm});
            skLineSegment(sketch, "E220.105", {"start": v(-8.71, -29.74) * mm, "end": v(-6.93, -29.18) * mm});
            skLineSegment(sketch, "E220.106", {"start": v(-10.34, -30.22) * mm, "end": v(-8.71, -29.74) * mm});
            skLineSegment(sketch, "E220.107", {"start": v(-11.87, -30.57) * mm, "end": v(-10.34, -30.22) * mm});
            skLineSegment(sketch, "E220.115", {"start": v(-31.15, -34.6) * mm, "end": v(-31.65, -32.83) * mm});
            skLineSegment(sketch, "E220.116", {"start": v(-31.65, -32.83) * mm, "end": v(-31.74, -31.35) * mm});
            skLineSegment(sketch, "E220.117", {"start": v(-31.74, -31.35) * mm, "end": v(-31.74, -29.94) * mm});
            skLineSegment(sketch, "E220.119", {"start": v(-22.5, -28.37) * mm, "end": v(-22.5, -28.8) * mm});
            skLineSegment(sketch, "E220.120", {"start": v(-22.5, -28.8) * mm, "end": v(-21.7, -29.4) * mm});
            skLineSegment(sketch, "E220.121", {"start": v(-21.7, -29.4) * mm, "end": v(-21.28, -29.63) * mm});
            skLineSegment(sketch, "E220.122", {"start": v(-21.28, -29.63) * mm, "end": v(-20.42, -29.92) * mm});
            skLineSegment(sketch, "E220.123", {"start": v(-20.42, -29.92) * mm, "end": v(-19.42, -30.26) * mm});
            skLineSegment(sketch, "E220.124", {"start": v(-19.42, -30.26) * mm, "end": v(-18.53, -30.48) * mm});
            skLineSegment(sketch, "E220.125", {"start": v(-18.53, -30.48) * mm, "end": v(-17.04, -30.69) * mm});
            skLineSegment(sketch, "E220.126", {"start": v(-17.04, -30.69) * mm, "end": v(-15.56, -30.84) * mm});
            skLineSegment(sketch, "E220.127", {"start": v(-15.56, -30.84) * mm, "end": v(-13.96, -30.84) * mm});
            skLineSegment(sketch, "E220.128", {"start": v(-13.96, -30.84) * mm, "end": v(-13.62, -30.84) * mm});
            skLineSegment(sketch, "E220.129", {"start": v(-13.62, -30.84) * mm, "end": v(-11.87, -30.57) * mm});
            skLineSegment(sketch, "E220.130", {"start": v(0.65, -54.54) * mm, "end": v(1.8, -54.85) * mm});
            skLineSegment(sketch, "E220.131", {"start": v(1.8, -54.85) * mm, "end": v(2.85, -55.25) * mm});
            skLineSegment(sketch, "E220.132", {"start": v(2.85, -55.25) * mm, "end": v(4.1, -55.84) * mm});
            skLineSegment(sketch, "E220.133", {"start": v(4.1, -55.84) * mm, "end": v(5.37, -56.77) * mm});
            skLineSegment(sketch, "E220.134", {"start": v(5.37, -56.77) * mm, "end": v(6.5, -58.2) * mm});
            skLineSegment(sketch, "E220.135", {"start": v(6.5, -58.2) * mm, "end": v(6.85, -59.38) * mm});
            skLineSegment(sketch, "E220.136", {"start": v(6.85, -59.38) * mm, "end": v(7.24, -60.7) * mm});
            skLineSegment(sketch, "E220.137", {"start": v(7.24, -60.7) * mm, "end": v(7.24, -62.66) * mm});
            skLineSegment(sketch, "E220.138", {"start": v(7.24, -62.66) * mm, "end": v(7.03, -64.47) * mm});
            skLineSegment(sketch, "E220.139", {"start": v(7.03, -64.47) * mm, "end": v(6.47, -66) * mm});
            skLineSegment(sketch, "E220.140", {"start": v(6.47, -66) * mm, "end": v(5.66, -67.36) * mm});
            skLineSegment(sketch, "E220.141", {"start": v(5.66, -67.36) * mm, "end": v(4.58, -68.43) * mm});
            skLineSegment(sketch, "E220.142", {"start": v(4.58, -68.43) * mm, "end": v(3.56, -69.12) * mm});
            skLineSegment(sketch, "E220.143", {"start": v(3.56, -69.12) * mm, "end": v(2.25, -70.1) * mm});
            skLineSegment(sketch, "E220.144", {"start": v(2.25, -70.1) * mm, "end": v(1.03, -70.28) * mm});
            skLineSegment(sketch, "E220.145", {"start": v(1.03, -70.28) * mm, "end": v(-0.75, -70.28) * mm});
            skLineSegment(sketch, "E220.146", {"start": v(-0.75, -70.28) * mm, "end": v(-2.13, -69.25) * mm});
            skLineSegment(sketch, "E220.147", {"start": v(-2.13, -69.25) * mm, "end": v(-2.16, -69.6) * mm});
            skLineSegment(sketch, "E220.148", {"start": v(-2.16, -69.6) * mm, "end": v(-2.48, -71.88) * mm});
            skLineSegment(sketch, "E220.149", {"start": v(-2.48, -71.88) * mm, "end": v(-2.62, -73.13) * mm});
            skLineSegment(sketch, "E220.150", {"start": v(-2.62, -73.13) * mm, "end": v(-2.62, -74.67) * mm});
            skLineSegment(sketch, "E220.151", {"start": v(-2.62, -74.67) * mm, "end": v(-2.32, -77.26) * mm});
            skLineSegment(sketch, "E220.152", {"start": v(-2.32, -77.26) * mm, "end": v(-1.97, -78.48) * mm});
            skLineSegment(sketch, "E220.153", {"start": v(-1.97, -78.48) * mm, "end": v(-1.66, -79.2) * mm});
            skLineSegment(sketch, "E220.154", {"start": v(-1.66, -79.2) * mm, "end": v(-1.11, -79.71) * mm});
            skLineSegment(sketch, "E220.155", {"start": v(-1.11, -79.71) * mm, "end": v(0.07, -80.59) * mm});
            skLineSegment(sketch, "E220.156", {"start": v(0.07, -80.59) * mm, "end": v(1.15, -81.2) * mm});
            skLineSegment(sketch, "E220.157", {"start": v(1.15, -81.2) * mm, "end": v(1.92, -81.4) * mm});
            skLineSegment(sketch, "E220.158", {"start": v(1.92, -81.4) * mm, "end": v(2.5, -81.46) * mm});
            skLineSegment(sketch, "E220.159", {"start": v(2.5, -81.46) * mm, "end": v(3.81, -81.17) * mm});
            skLineSegment(sketch, "E220.160", {"start": v(3.81, -81.17) * mm, "end": v(4.5, -80.9) * mm});
            skLineSegment(sketch, "E220.161", {"start": v(4.5, -80.9) * mm, "end": v(5.3, -80.41) * mm});
            skLineSegment(sketch, "E220.162", {"start": v(5.3, -80.41) * mm, "end": v(6.1, -79.67) * mm});
            skLineSegment(sketch, "E220.163", {"start": v(6.1, -79.67) * mm, "end": v(6.82, -78.74) * mm});
            skLineSegment(sketch, "E220.164", {"start": v(6.82, -78.74) * mm, "end": v(7.88, -77.53) * mm});
            skLineSegment(sketch, "E220.165", {"start": v(7.88, -77.53) * mm, "end": v(9.95, -76.34) * mm});
            skLineSegment(sketch, "E220.166", {"start": v(9.95, -76.34) * mm, "end": v(12.14, -76.34) * mm});
            skLineSegment(sketch, "E220.167", {"start": v(12.14, -76.34) * mm, "end": v(14.02, -77.11) * mm});
            skLineSegment(sketch, "E220.168", {"start": v(14.02, -77.11) * mm, "end": v(14.98, -78.39) * mm});
            skLineSegment(sketch, "E221", {"start": v(-31.74, -29.94) * mm, "end": v(-30.4, -28.96) * mm});
            skPoint(sketch, "E221.endSnap0", {"position": v(-28.34, -28.96) * mm});
            skLineSegment(sketch, "E222", {"start": v(-30.4, -28.96) * mm, "end": v(-29, -28.3) * mm});
            skLineSegment(sketch, "E223", {"start": v(-29, -28.3) * mm, "end": v(-27.9, -27.88) * mm});
            skLineSegment(sketch, "E224", {"start": v(-27.9, -27.88) * mm, "end": v(-26.86, -27.64) * mm});
            skLineSegment(sketch, "E225", {"start": v(-26.2, -27.64) * mm, "end": v(-24.55, -27.32) * mm});
            skLineSegment(sketch, "E226", {"start": v(-24.55, -27.32) * mm, "end": v(-23.22, -27.23) * mm});
            skLineSegment(sketch, "E227", {"start": v(-5.83, -28.73) * mm, "end": v(-4.95, -29.12) * mm});
            skLineSegment(sketch, "E228", {"start": v(-4.95, -29.12) * mm, "end": v(-4.15, -29.5) * mm});
            skLineSegment(sketch, "E229", {"start": v(-4.15, -29.5) * mm, "end": v(-3.32, -29.92) * mm});
            skLineSegment(sketch, "E230", {"start": v(-3.32, -29.92) * mm, "end": v(-2.62, -30.35) * mm});
            skLineSegment(sketch, "E231", {"start": v(4.16, -35.94) * mm, "end": v(3.77, -35.53) * mm});
            skLineSegment(sketch, "E232", {"start": v(3.77, -35.53) * mm, "end": v(3.08, -34.84) * mm});
            skLineSegment(sketch, "E233", {"start": v(3.08, -34.84) * mm, "end": v(2.3, -34.16) * mm});
            skLineSegment(sketch, "E234", {"start": v(2.3, -34.16) * mm, "end": v(1.87, -33.88) * mm});
            skLineSegment(sketch, "E235", {"start": v(-22.8, -27.18) * mm, "end": v(-23.22, -27.23) * mm});
            skLineSegment(sketch, "E236", {"start": v(-31.15, -34.6) * mm, "end": v(-30.26, -36.16) * mm});
            skLineSegment(sketch, "E237", {"start": v(-22.8, -27.18) * mm, "end": v(-22.5, -28.37) * mm});
            skLineSegment(sketch, "E238", {"start": v(-57.1, -74.38) * mm, "end": v(-57.1, -75.99) * mm});
            skLineSegment(sketch, "E239", {"start": v(-57.1, -75.99) * mm, "end": v(-57.11, -77.48) * mm});
            skLineSegment(sketch, "E240", {"start": v(-57.11, -77.48) * mm, "end": v(-56.78, -79.16) * mm});
            skLineSegment(sketch, "E241", {"start": v(-47.7, -94.72) * mm, "end": v(-48.86, -93.93) * mm});
            skLineSegment(sketch, "E242", {"start": v(-48.86, -93.93) * mm, "end": v(-49.84, -93.2) * mm});
            skLineSegment(sketch, "E243", {"start": v(-49.84, -93.2) * mm, "end": v(-50.82, -92.23) * mm});
            skLineSegment(sketch, "E244", {"start": v(-50.82, -92.23) * mm, "end": v(-52.08, -90.99) * mm});
            skLineSegment(sketch, "E245", {"start": v(-52.08, -90.99) * mm, "end": v(-53.3, -89.44) * mm});
            skLineSegment(sketch, "E246", {"start": v(-53.3, -89.44) * mm, "end": v(-54.82, -87.41) * mm});
            skLineSegment(sketch, "E247", {"start": v(-0.24, -95.5) * mm, "end": v(1.85, -94.37) * mm});
            skLineSegment(sketch, "E248", {"start": v(1.85, -94.37) * mm, "end": v(4.07, -92.81) * mm});
            skLineSegment(sketch, "E249", {"start": v(4.07, -92.81) * mm, "end": v(6.74, -90.8) * mm});
            skLineSegment(sketch, "E250", {"start": v(6.74, -90.8) * mm, "end": v(7.21, -90.23) * mm});
            skLineSegment(sketch, "E251", {"start": v(14.98, -78.39) * mm, "end": v(14.43, -79.5) * mm});
            skLineSegment(sketch, "E252", {"start": v(14.43, -79.5) * mm, "end": v(13.68, -81.13) * mm});
            skLineSegment(sketch, "E253", {"start": v(13.68, -81.13) * mm, "end": v(13.1, -82.44) * mm});
            skSolve(sketch);
        }
        {
            var Q0;
            Q0=makeQuery(id+"F0.imprint","IMPRINT",FACE,{"disambiguationData":[TD([[makeQuery(id+"F0.imprint","IMPRINT",EDGE,{"derivedFrom":sQuery(id+"F0.wireOp",EDGE,"E0")}),-1.0]])]});
            extrude(context, id + "F1", {"entities" : qUnion([Q0]), "depth" : 29 * mm});
        }
        {
            var Q0;
            Q0=makeQuery(id+"F0.imprint","IMPRINT",FACE,{"disambiguationData":[TD([[makeQuery(id+"F0.imprint","IMPRINT",EDGE,{"derivedFrom":sQuery(id+"F0.wireOp",EDGE,"E178")}),1.0]])]});
            extrude(context, id + "F2", {"entities" : qUnion([Q0]), "depth" : 25.4 * mm, "hasSecondDirection" : true, "secondDirectionOppositeDirection" : false, "secondDirectionDepth" : 3 * mm});
        }
        {
            var Q0;
            Q0=makeQuery(id+"F0.imprint","IMPRINT",FACE,{"disambiguationData":[TD([[makeQuery(id+"F0.imprint","IMPRINT",EDGE,{"derivedFrom":sQuery(id+"F0.wireOp",EDGE,"E104")}),1.0]])]});
            var Q1;
            Q1=makeQuery(id+"F0.imprint","IMPRINT",FACE,{"disambiguationData":[TD([[makeQuery(id+"F0.imprint","IMPRINT",EDGE,{"derivedFrom":sQuery(id+"F0.wireOp",EDGE,"E78")}),1.0]])]});
            var Q2;
            Q2=makeQuery(id+"F0.imprint","IMPRINT",FACE,{"disambiguationData":[TD([[makeQuery(id+"F0.imprint","IMPRINT",EDGE,{"derivedFrom":sQuery(id+"F0.wireOp",EDGE,"E0")}),1.0]])]});
            extrude(context, id + "F3", {"entities" : qUnion([Q0, Q1, Q2]), "depth" : 25 * mm, "hasSecondDirection" : true, "secondDirectionOppositeDirection" : false, "secondDirectionDepth" : 3 * mm});
        }
    });
